# Revit family: 0047670
name_source: partatom
category: Lighting Fixtures
revit_build: Autodesk Revit 2017 (Build: 20160225_1515(x64)
units: mm (PartAtom-declared; Revit-internal decimal feet)

## family parameters
Cut with Voids When Loaded = No
Host = Face
Light Source = Yes
OmniClass Number = 23.80.70.00
OmniClass Title = Lighting
Part Type = Normal
Room Calculation Point = No
Round Connector Dimension = Use Diameter
Shared = No

## types (1)
- 0047670 START ECO PANEL 600X600 3200LM 840
    Apparent Load = 36 VA
    Assembly Code = D5020200
    AssetType = Fixed
    ClassificationName = Uniclass2015
    ClassificationValue = EF_70_80
    Color Filter = 16777215
    Cost = 0 $
    Default Elevation = 1219 mm
    Dimming Lamp Color Temperature Shift = <None>
    DocumentationLiterature = http://www.sylvania-lighting.com
    ElectricShockClassification = Class II
    Emit Shape Visible in Rendering = No
    Emit from Rectangle Length = 553 mm  [stored 1.8143 ft]
    Emit from Rectangle Width = 553 mm  [stored 1.8143 ft]
    IfcExportAs = IfcLightFixtureType
    IfcExportType = IfcLightFixtureType
    ImpactProtectionIndex = IK03
    IngressProtection = IP40/20
    Keynote = 16500
    Lamp = LED
    LampColourRenderingIndex = 80
    LampColourTemperature = 4000 K
    LampMacAdamStep = 6
    LampNominalLuminous = 3200 lm
    LampsType = LED
    LuminousEfficacy = 89 lm/W
    Manufacturer = Feilo Sylvania
    ManufacturerName = Feilo Sylvania
    Material = al 6063 housing, ps diffuser
    Material_1_SYL = PC/ABS Plastic
    Material_2_SYL = LED
    Material_3_SYL = <By Category>
    Material_4_SYL = <By Category>
    Model = START eco Panel 600x600 3200Lm 840
    ModelNumber = 0047670
    ModelReference = START eco Panel 600x600 3200Lm 840
    Name = START eco Panel 600x600 3200Lm 840
    NominalDepth = 595 mm  [stored 1.9521 ft]
    NominalHeight = 34 mm
    NominalLength = 595 mm  [stored 1.9521 ft]
    Photometric Web File = 0047670.ies
    PowerConsumption = 36 W
    PowerFactor = 0.95
    Tilt Angle = -90.00°
    Type Image = <None>
    TypeName = START eco Panel 600x600 3200Lm 840
    URL = http://www.sylvania-lighting.com
    Voltage = 0 V

note: [stored X ft] marks values corroborated as IEEE doubles in the binary element streams (Revit-internal decimal feet)

## geometry (parser evidence)
native form markers: Sweep x3
no freeform markers — native parametric forms only
